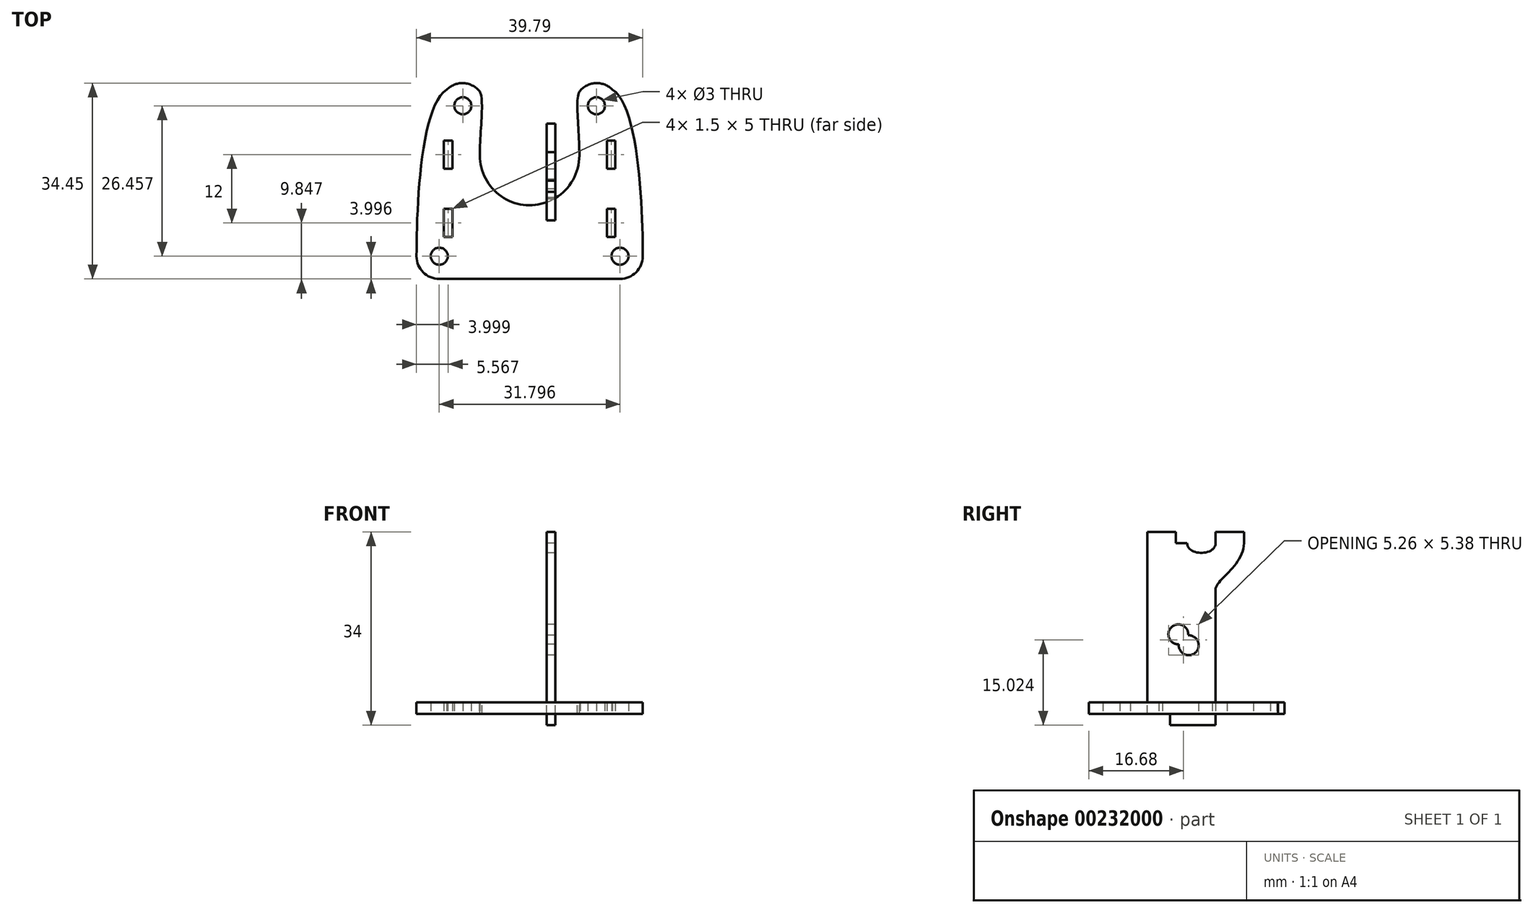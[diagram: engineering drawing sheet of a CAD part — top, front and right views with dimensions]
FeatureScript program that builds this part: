
annotation { "Feature Type Name" : "Feature", "Feature Type Description" : "" }
export const myFeature = defineFeature(function(context is Context, id is Id, definition is map)
    precondition{}
    {
        {
            var Q0;
            Q0=qCreatedBy(makeId("Right.planeOp"),FACE);
            var sketch = newSketch(context, id + "F0", { "sketchPlane" : qUnion([Q0])});
            skLineSegment(sketch, "E0", {"start": v(30.57, 0) * mm, "end": v(30.57, -2) * mm});
            skLineSegment(sketch, "E1", {"start": v(30.57, -2) * mm, "end": v(22.57, -2) * mm});
            skLineSegment(sketch, "E2", {"start": v(22.57, -2) * mm, "end": v(22.57, 0) * mm});
            skLineSegment(sketch, "E3", {"start": v(22.57, 0) * mm, "end": v(18.57, 0) * mm});
            skLineSegment(sketch, "E4", {"start": v(18.57, 30) * mm, "end": v(18.57, 0) * mm});
            skArc(sketch, "E5", {"start": v(24.11, 12.24) * mm, "mid": v(27.06, 10.8) * mm, "end": v(25.77, 13.81) * mm});
            skPoint(sketch, "E5.centerSnap0", {"position": v(18.57, 15) * mm});
            skPoint(sketch, "E5.centerSnap1", {"position": v(26.57, 32) * mm});
            skArc(sketch, "E6", {"start": v(25.77, 13.81) * mm, "mid": v(22.82, 15.25) * mm, "end": v(24.11, 12.24) * mm});
            skLineSegment(sketch, "E7", {"start": v(18.57, 30) * mm, "end": v(18.57, 32) * mm});
            skLineSegment(sketch, "E8", {"start": v(18.57, 32) * mm, "end": v(23.57, 32) * mm});
            skLineSegment(sketch, "E9", {"start": v(30.57, 21.84) * mm, "end": v(30.57, 0) * mm});
            skFitSpline(sketch, "E10", {"points": [v(30.57, 30) * mm, v(25.57, 30) * mm], "startDerivative": vector(0, -6.72) * mm, "endDerivative": vector(0, 6.72) * mm});
            skLineSegment(sketch, "E11", {"start": v(27.95, 30) * mm, "end": v(27.95, 28) * mm, "construction": true});
            skLineSegment(sketch, "E12", {"start": v(30.57, 27.76) * mm, "end": v(25.57, 27.76) * mm, "construction": true});
            skLineSegment(sketch, "E13", {"start": v(30.57, 30) * mm, "end": v(30.57, 32) * mm});
            skLineSegment(sketch, "E14", {"start": v(30.57, 32) * mm, "end": v(35.57, 32) * mm});
            skLineSegment(sketch, "E15", {"start": v(35.57, 32) * mm, "end": v(35.57, 30) * mm});
            skFitSpline(sketch, "E16", {"points": [v(35.57, 30) * mm, v(30.57, 21.84) * mm], "startDerivative": vector(0, -11.6) * mm, "endDerivative": vector(0, -5.4) * mm});
            skLineSegment(sketch, "E17", {"start": v(23.57, 32) * mm, "end": v(23.57, 30) * mm});
            skLineSegment(sketch, "E18", {"start": v(23.57, 30) * mm, "end": v(25.57, 30) * mm});
            skPoint(sketch, "E19", {"position": v(25.77, 13.81) * mm});
            skPoint(sketch, "E20", {"position": v(24.11, 12.24) * mm});
            skSolve(sketch);
        }
        {
            var Q0;
            Q0 = qSketchRegion(id + "F0", true);
            extrude(context, id + "F1", {"entities" : qUnion([Q0]), "depth" : 1.5 * mm});
        }
        {
            var Q0;
            Q0=qCreatedBy(makeId("Top.planeOp"),FACE);
            var sketch = newSketch(context, id + "F2", { "sketchPlane" : qUnion([Q0])});
            skPoint(sketch, "E21.middle", {"position": v(-3.02, -2.3) * mm});
            skLineSegment(sketch, "E22.bottom", {"start": v(22.68, 30.32) * mm, "end": v(-28.72, 30.32) * mm, "construction": true});
            skLineSegment(sketch, "E22.top", {"start": v(22.68, -34.92) * mm, "end": v(-28.72, -34.92) * mm, "construction": true});
            skLineSegment(sketch, "E22.left", {"start": v(22.68, 30.32) * mm, "end": v(22.68, -34.92) * mm, "construction": true});
            skLineSegment(sketch, "E22.right", {"start": v(-28.72, 30.32) * mm, "end": v(-28.72, -34.92) * mm, "construction": true});
            skLineSegment(sketch, "E23.bottom", {"start": v(-68.02, 80.2) * mm, "end": v(61.98, 80.2) * mm, "construction": true});
            skLineSegment(sketch, "E23.top", {"start": v(-68.02, -84.8) * mm, "end": v(61.98, -84.8) * mm, "construction": true});
            skLineSegment(sketch, "E23.left", {"start": v(-68.02, 80.2) * mm, "end": v(-68.02, -84.8) * mm, "construction": true});
            skLineSegment(sketch, "E23.right", {"start": v(61.98, 80.2) * mm, "end": v(61.98, -84.8) * mm, "construction": true});
            skCircle(sketch, "E24", {"center": v(61.98, 80.2) * mm, "radius": 4.5 * mm, "construction": true});
            skCircle(sketch, "E25", {"center": v(-68.02, 80.2) * mm, "radius": 4.5 * mm, "construction": true});
            skCircle(sketch, "E26", {"center": v(61.98, -84.8) * mm, "radius": 4.5 * mm, "construction": true});
            skCircle(sketch, "E27", {"center": v(-68.02, -84.8) * mm, "radius": 4.5 * mm, "construction": true});
            skCircle(sketch, "E28", {"center": v(61.98, 80.2) * mm, "radius": 8 * mm, "construction": true});
            skCircle(sketch, "E29", {"center": v(61.98, -84.8) * mm, "radius": 8 * mm, "construction": true});
            skCircle(sketch, "E30", {"center": v(-68.02, -84.8) * mm, "radius": 8 * mm, "construction": true});
            skCircle(sketch, "E31", {"center": v(-68.02, 80.2) * mm, "radius": 8 * mm, "construction": true});
            skCircle(sketch, "E32", {"center": v(61.98, 80.2) * mm, "radius": 9.5 * mm, "construction": true});
            skCircle(sketch, "E33", {"center": v(61.98, -84.8) * mm, "radius": 9.5 * mm, "construction": true});
            skCircle(sketch, "E34", {"center": v(-68.02, -84.8) * mm, "radius": 9.5 * mm, "construction": true});
            skCircle(sketch, "E35", {"center": v(-68.02, 80.2) * mm, "radius": 9.5 * mm, "construction": true});
            skCircle(sketch, "E36", {"center": v(61.98, 80.2) * mm, "radius": 14 * mm, "construction": true});
            skCircle(sketch, "E37", {"center": v(-68.02, 80.2) * mm, "radius": 14 * mm, "construction": true});
            skCircle(sketch, "E38", {"center": v(61.98, -84.8) * mm, "radius": 14 * mm, "construction": true});
            skCircle(sketch, "E39", {"center": v(-68.02, -84.8) * mm, "radius": 14 * mm, "construction": true});
            skCircle(sketch, "E40", {"center": v(61.98, 80.2) * mm, "radius": 63.5 * mm, "construction": true});
            skCircle(sketch, "E41", {"center": v(61.98, -84.8) * mm, "radius": 63.5 * mm, "construction": true});
            skCircle(sketch, "E42", {"center": v(-68.02, -84.8) * mm, "radius": 63.5 * mm, "construction": true});
            skCircle(sketch, "E43", {"center": v(-68.02, 80.2) * mm, "radius": 63.5 * mm, "construction": true});
            skLineSegment(sketch, "E44.bottom", {"start": v(-29.21, 23.9) * mm, "end": v(23.17, 23.9) * mm, "construction": true});
            skLineSegment(sketch, "E44.top", {"start": v(-29.21, -28.49) * mm, "end": v(23.17, -28.49) * mm, "construction": true});
            skLineSegment(sketch, "E44.left", {"start": v(-29.21, 23.9) * mm, "end": v(-29.21, -28.49) * mm, "construction": true});
            skLineSegment(sketch, "E44.right", {"start": v(23.17, 23.9) * mm, "end": v(23.17, -28.49) * mm, "construction": true});
            skCircle(sketch, "E45", {"center": v(22.68, 30.32) * mm, "radius": 1.5 * mm, "construction": true});
            skCircle(sketch, "E46", {"center": v(-28.72, 30.32) * mm, "radius": 1.5 * mm, "construction": true});
            skCircle(sketch, "E47", {"center": v(22.68, -34.92) * mm, "radius": 1.5 * mm, "construction": true});
            skCircle(sketch, "E48", {"center": v(-28.72, -34.92) * mm, "radius": 1.5 * mm, "construction": true});
            skLineSegment(sketch, "E49", {"start": v(-68.02, 80.2) * mm, "end": v(61.98, -84.8) * mm, "construction": true});
            skLineSegment(sketch, "E50", {"start": v(61.98, 80.2) * mm, "end": v(-68.02, -84.8) * mm, "construction": true});
            skLineSegment(sketch, "E51.bottom", {"start": v(-18.27, -7.32) * mm, "end": v(12.23, -7.32) * mm, "construction": true});
            skLineSegment(sketch, "E51.top", {"start": v(-18.27, -37.82) * mm, "end": v(12.23, -37.82) * mm, "construction": true});
            skLineSegment(sketch, "E51.left", {"start": v(-18.27, -7.32) * mm, "end": v(-18.27, -37.82) * mm, "construction": true});
            skLineSegment(sketch, "E51.right", {"start": v(12.23, -7.32) * mm, "end": v(12.23, -37.82) * mm, "construction": true});
            skPoint(sketch, "E51.middle", {"position": v(-3.02, -22.57) * mm});
            skLineSegment(sketch, "E52.bottom", {"start": v(-18.27, 29.18) * mm, "end": v(12.23, 29.18) * mm, "construction": true});
            skLineSegment(sketch, "E52.top", {"start": v(-18.27, -1.32) * mm, "end": v(12.23, -1.32) * mm, "construction": true});
            skLineSegment(sketch, "E52.left", {"start": v(-18.27, 29.18) * mm, "end": v(-18.27, -1.32) * mm, "construction": true});
            skLineSegment(sketch, "E52.right", {"start": v(12.23, 29.18) * mm, "end": v(12.23, -1.32) * mm, "construction": true});
            skPoint(sketch, "E52.middle", {"position": v(-3.02, 13.93) * mm});
            skLineSegment(sketch, "E53", {"start": v(-3.02, -1.32) * mm, "end": v(-3.02, -7.32) * mm, "construction": true});
            skLineSegment(sketch, "E54", {"start": v(-3.02, 38.71) * mm, "end": v(-14.77, 38.71) * mm, "construction": true});
            skLineSegment(sketch, "E55", {"start": v(-3.02, 38.71) * mm, "end": v(8.73, 38.71) * mm, "construction": true});
            skLineSegment(sketch, "E56", {"start": v(-28.72, 30.32) * mm, "end": v(-23.23, 34.65) * mm, "construction": true});
            skLineSegment(sketch, "E57", {"start": v(-28.72, 30.32) * mm, "end": v(-34.22, 25.99) * mm, "construction": true});
            skLineSegment(sketch, "E58", {"start": v(-28.72, 30.32) * mm, "end": v(-33.06, 35.82) * mm, "construction": true});
            skLineSegment(sketch, "E59", {"start": v(22.68, 30.32) * mm, "end": v(27.01, 35.82) * mm, "construction": true});
            skLineSegment(sketch, "E60", {"start": v(22.68, 30.32) * mm, "end": v(17.18, 34.65) * mm, "construction": true});
            skLineSegment(sketch, "E61", {"start": v(22.68, 30.32) * mm, "end": v(28.18, 25.99) * mm, "construction": true});
            skLineSegment(sketch, "E62", {"start": v(22.68, -34.92) * mm, "end": v(27.01, -40.42) * mm, "construction": true});
            skLineSegment(sketch, "E63", {"start": v(22.68, -34.92) * mm, "end": v(17.18, -39.25) * mm, "construction": true});
            skLineSegment(sketch, "E64", {"start": v(22.68, -34.92) * mm, "end": v(28.18, -30.59) * mm, "construction": true});
            skLineSegment(sketch, "E65", {"start": v(-28.72, -34.92) * mm, "end": v(-33.06, -40.42) * mm, "construction": true});
            skLineSegment(sketch, "E66", {"start": v(-28.72, -34.92) * mm, "end": v(-23.23, -39.25) * mm, "construction": true});
            skLineSegment(sketch, "E67", {"start": v(-28.72, -34.92) * mm, "end": v(-34.22, -30.59) * mm, "construction": true});
            skFitSpline(sketch, "E68", {"points": [v(-23.23, 34.65) * mm, v(-33.06, 35.82) * mm, v(-34.22, 25.99) * mm], "startDerivative": vector(-20.3, 7.46) * mm, "endDerivative": vector(0.93, -21.61) * mm});
            skFitSpline(sketch, "E69", {"points": [v(17.18, 34.65) * mm, v(27.01, 35.82) * mm, v(28.18, 25.99) * mm], "startDerivative": vector(20.3, 7.46) * mm, "endDerivative": vector(-0.93, -21.61) * mm});
            skFitSpline(sketch, "E70", {"points": [v(28.18, -30.59) * mm, v(27.01, -40.42) * mm, v(17.18, -39.25) * mm], "startDerivative": vector(0.93, -21.61) * mm, "endDerivative": vector(-20.3, 7.46) * mm});
            skFitSpline(sketch, "E71", {"points": [v(-23.23, -39.25) * mm, v(-33.06, -40.42) * mm, v(-34.22, -30.59) * mm], "startDerivative": vector(-20.3, -7.46) * mm, "endDerivative": vector(0.93, 21.61) * mm});
            skLineSegment(sketch, "E72", {"start": v(-14.77, 38.71) * mm, "end": v(-18.77, 38.71) * mm, "construction": true});
            skLineSegment(sketch, "E73", {"start": v(8.73, 38.71) * mm, "end": v(12.73, 38.71) * mm, "construction": true});
            skCircle(sketch, "E74", {"center": v(-14.77, 38.71) * mm, "radius": 1.5 * mm});
            skCircle(sketch, "E75", {"center": v(8.73, 38.71) * mm, "radius": 1.5 * mm});
            skLineSegment(sketch, "E76", {"start": v(-3.02, 38.71) * mm, "end": v(-3.02, 42.71) * mm, "construction": true});
            skLineSegment(sketch, "E77", {"start": v(-18.77, 38.71) * mm, "end": v(-18.77, 38.71) * mm});
            skLineSegment(sketch, "E78", {"start": v(-14.77, 42.71) * mm, "end": v(-3.02, 42.71) * mm});
            skLineSegment(sketch, "E79", {"start": v(-3.02, 42.71) * mm, "end": v(8.73, 42.71) * mm});
            skLineSegment(sketch, "E80", {"start": v(12.73, 38.71) * mm, "end": v(12.73, 38.71) * mm});
            skPoint(sketch, "E81.visualSharp", {"position": v(-18.77, 42.71) * mm});
            skArc(sketch, "E81.filletArc", {"start": v(-14.77, 42.71) * mm, "mid": v(-17.6, 41.54) * mm, "end": v(-18.77, 38.71) * mm});
            skPoint(sketch, "E82.visualSharp", {"position": v(12.73, 42.71) * mm});
            skArc(sketch, "E82.filletArc", {"start": v(12.73, 38.71) * mm, "mid": v(11.56, 41.54) * mm, "end": v(8.73, 42.71) * mm});
            skLineSegment(sketch, "E83", {"start": v(-23.23, 34.65) * mm, "end": v(-21.36, 34.08) * mm});
            skLineSegment(sketch, "E84", {"start": v(-18.77, 36) * mm, "end": v(-18.77, 38.71) * mm});
            skPoint(sketch, "E85.visualSharp", {"position": v(-18.77, 33.29) * mm});
            skArc(sketch, "E85.filletArc", {"start": v(-21.36, 34.08) * mm, "mid": v(-19.58, 34.38) * mm, "end": v(-18.77, 36) * mm});
            skLineSegment(sketch, "E86", {"start": v(-18.77, 33.29) * mm, "end": v(-3.02, 33.29) * mm, "construction": true});
            skLineSegment(sketch, "E87", {"start": v(-3.02, 33.29) * mm, "end": v(12.73, 33.29) * mm, "construction": true});
            skLineSegment(sketch, "E88", {"start": v(17.18, 34.65) * mm, "end": v(15.31, 34.08) * mm});
            skLineSegment(sketch, "E89", {"start": v(12.73, 38.71) * mm, "end": v(12.73, 36) * mm});
            skPoint(sketch, "E90.visualSharp", {"position": v(12.73, 33.29) * mm});
            skArc(sketch, "E90.filletArc", {"start": v(12.73, 36) * mm, "mid": v(13.54, 34.38) * mm, "end": v(15.31, 34.08) * mm});
            skCircle(sketch, "E91", {"center": v(-18.27, -37.82) * mm, "radius": 1.5 * mm});
            skCircle(sketch, "E92", {"center": v(12.23, -37.82) * mm, "radius": 1.5 * mm});
            skLineSegment(sketch, "E93", {"start": v(-3.02, -37.82) * mm, "end": v(-3.02, -41.82) * mm, "construction": true});
            skLineSegment(sketch, "E94", {"start": v(-18.27, -37.82) * mm, "end": v(-22.27, -37.82) * mm, "construction": true});
            skLineSegment(sketch, "E95", {"start": v(12.23, -37.82) * mm, "end": v(16.23, -37.82) * mm, "construction": true});
            skLineSegment(sketch, "E96", {"start": v(-22.27, -40.76) * mm, "end": v(-3.02, -40.76) * mm, "construction": true});
            skLineSegment(sketch, "E97", {"start": v(-3.02, -40.76) * mm, "end": v(16.23, -40.76) * mm, "construction": true});
            skPoint(sketch, "E98.visualSharp", {"position": v(-22.27, -40.76) * mm});
            skPoint(sketch, "E99.visualSharp", {"position": v(16.23, -40.76) * mm});
            skCircle(sketch, "E100", {"center": v(-12.82, -47.2) * mm, "radius": 1.5 * mm});
            skCircle(sketch, "E101", {"center": v(6.78, -47.2) * mm, "radius": 1.5 * mm});
            skLineSegment(sketch, "E102", {"start": v(-12.82, -47.2) * mm, "end": v(-3.02, -47.2) * mm, "construction": true});
            skLineSegment(sketch, "E103", {"start": v(-3.02, -47.2) * mm, "end": v(6.78, -47.2) * mm, "construction": true});
            skFitSpline(sketch, "E104", {"points": [v(-34.22, 25.99) * mm, v(-28.72, -2.3) * mm, v(-34.22, -30.59) * mm], "startDerivative": vector(16.96, -67.18) * mm, "endDerivative": vector(-16.96, -67.18) * mm});
            skFitSpline(sketch, "E105", {"points": [v(28.18, 25.99) * mm, v(22.68, -2.3) * mm, v(28.18, -30.59) * mm], "startDerivative": vector(-16.96, -67.18) * mm, "endDerivative": vector(16.96, -67.18) * mm});
            skLineSegment(sketch, "E106", {"start": v(-3.02, -47.2) * mm, "end": v(-3.02, -53.2) * mm, "construction": true});
            skLineSegment(sketch, "E107", {"start": v(-12.82, -47.2) * mm, "end": v(-16.82, -47.2) * mm, "construction": true});
            skLineSegment(sketch, "E108", {"start": v(-12.82, -47.2) * mm, "end": v(-12.82, -51.2) * mm, "construction": true});
            skLineSegment(sketch, "E109", {"start": v(6.78, -47.2) * mm, "end": v(10.78, -47.2) * mm, "construction": true});
            skLineSegment(sketch, "E110", {"start": v(6.78, -47.2) * mm, "end": v(6.78, -51.2) * mm, "construction": true});
            skCircle(sketch, "E111", {"center": v(-28.72, 30.32) * mm, "radius": 1.5 * mm});
            skCircle(sketch, "E112", {"center": v(22.68, 30.32) * mm, "radius": 1.5 * mm});
            skCircle(sketch, "E113", {"center": v(-28.72, -34.92) * mm, "radius": 1.5 * mm});
            skCircle(sketch, "E114", {"center": v(22.68, -34.92) * mm, "radius": 1.5 * mm});
            skLineSegment(sketch, "E115", {"start": v(-3.02, 30.32) * mm, "end": v(-3.02, 38.71) * mm, "construction": true});
            skLineSegment(sketch, "E116", {"start": v(114.53, -26.93) * mm, "end": v(114.53, 7.03) * mm, "construction": true});
            skLineSegment(sketch, "E117", {"start": v(-22.07, -38.82) * mm, "end": v(-3.02, -38.82) * mm, "construction": true});
            skLineSegment(sketch, "E118", {"start": v(-3.02, -38.82) * mm, "end": v(16.02, -38.82) * mm, "construction": true});
            skFitSpline(sketch, "E119", {"points": [v(-22.27, -40.76) * mm, v(-16.82, -47.2) * mm, v(-12.82, -51.2) * mm, v(-3.02, -53.2) * mm], "startDerivative": vector(17.01, -18.5) * mm, "endDerivative": vector(29.8, -3.11) * mm});
            skFitSpline(sketch, "E120", {"points": [v(16.23, -40.76) * mm, v(10.78, -47.2) * mm, v(6.78, -51.2) * mm, v(-3.02, -53.2) * mm], "startDerivative": vector(-17.98, -19.6) * mm, "endDerivative": vector(-29.8, -3.11) * mm});
            skLineSegment(sketch, "E121", {"start": v(115.56, 8.03) * mm, "end": v(168.77, 6.38) * mm, "construction": true});
            skPoint(sketch, "E122.visualSharp", {"position": v(114.53, 8.07) * mm});
            skArc(sketch, "E122.filletArc", {"start": v(115.56, 8.03) * mm, "mid": v(114.83, 7.75) * mm, "end": v(114.53, 7.03) * mm, "construction": true});
            skPoint(sketch, "E123.visualSharp", {"position": v(16.02, -38.82) * mm});
            skPoint(sketch, "E124.visualSharp", {"position": v(-22.07, -38.82) * mm});
            skLineSegment(sketch, "E125.bottom", {"start": v(-16.8, 15.2) * mm, "end": v(10.76, 15.2) * mm, "construction": true});
            skLineSegment(sketch, "E125.top", {"start": v(-16.8, -19.8) * mm, "end": v(10.76, -19.8) * mm, "construction": true});
            skLineSegment(sketch, "E125.left", {"start": v(-16.8, 15.2) * mm, "end": v(-16.8, -19.8) * mm, "construction": true});
            skLineSegment(sketch, "E125.right", {"start": v(10.76, 15.2) * mm, "end": v(10.76, -19.8) * mm, "construction": true});
            skCircle(sketch, "E126", {"center": v(-18.27, -7.32) * mm, "radius": 1.5 * mm});
            skCircle(sketch, "E127", {"center": v(12.23, -7.32) * mm, "radius": 1.5 * mm});
            skCircle(sketch, "E128", {"center": v(12.23, -1.32) * mm, "radius": 1.5 * mm});
            skCircle(sketch, "E129", {"center": v(-18.27, -1.32) * mm, "radius": 1.5 * mm});
            skCircle(sketch, "E130", {"center": v(-18.27, 29.18) * mm, "radius": 1.5 * mm});
            skCircle(sketch, "E131", {"center": v(12.23, 29.18) * mm, "radius": 1.5 * mm});
            skFitSpline(sketch, "E132", {"points": [v(-23.23, -39.25) * mm, v(-22.27, -40.76) * mm], "startDerivative": vector(0.95, -1.5) * mm, "endDerivative": vector(0.95, -1.5) * mm});
            skFitSpline(sketch, "E133", {"points": [v(17.18, -39.25) * mm, v(16.23, -40.76) * mm], "startDerivative": vector(-0.95, -1.5) * mm, "endDerivative": vector(-0.95, -1.5) * mm});
            skLineSegment(sketch, "E134", {"start": v(-3.02, 10.77) * mm, "end": v(-21.23, 10.77) * mm, "construction": true});
            skLineSegment(sketch, "E135", {"start": v(-3.02, 10.77) * mm, "end": v(15.18, 10.77) * mm, "construction": true});
            skLineSegment(sketch, "E136", {"start": v(-3.02, -2.3) * mm, "end": v(-3.02, 11.97) * mm, "construction": true});
            skLineSegment(sketch, "E137", {"start": v(-3.02, -2.3) * mm, "end": v(10.3, -2.3) * mm, "construction": true});
            skLineSegment(sketch, "E138.bottom", {"start": v(-18.92, 12.26) * mm, "end": v(12.87, 12.26) * mm, "construction": true});
            skLineSegment(sketch, "E138.top", {"start": v(-18.92, -16.85) * mm, "end": v(12.87, -16.85) * mm, "construction": true});
            skLineSegment(sketch, "E138.left", {"start": v(-18.92, 12.26) * mm, "end": v(-18.92, -16.85) * mm, "construction": true});
            skLineSegment(sketch, "E138.right", {"start": v(12.87, 12.26) * mm, "end": v(12.87, -16.85) * mm, "construction": true});
            skCircle(sketch, "E139", {"center": v(12.87, 12.26) * mm, "radius": 1.5 * mm});
            skCircle(sketch, "E140", {"center": v(12.87, -16.85) * mm, "radius": 1.5 * mm});
            skCircle(sketch, "E141", {"center": v(-18.92, -16.85) * mm, "radius": 1.5 * mm});
            skCircle(sketch, "E142", {"center": v(-18.92, 12.26) * mm, "radius": 1.5 * mm});
            skLineSegment(sketch, "E143", {"start": v(-3.02, 23.62) * mm, "end": v(11.3, 23.62) * mm, "construction": true});
            skLineSegment(sketch, "E144", {"start": v(-3.02, 23.62) * mm, "end": v(-17.35, 23.62) * mm, "construction": true});
            skLineSegment(sketch, "E145.bottom", {"start": v(-18.1, 27.62) * mm, "end": v(-16.6, 27.62) * mm});
            skLineSegment(sketch, "E145.top", {"start": v(-18.1, 19.62) * mm, "end": v(-16.6, 19.62) * mm});
            skLineSegment(sketch, "E145.left", {"start": v(-18.1, 27.62) * mm, "end": v(-18.1, 19.62) * mm});
            skLineSegment(sketch, "E145.right", {"start": v(-16.6, 27.62) * mm, "end": v(-16.6, 19.62) * mm});
            skPoint(sketch, "E145.middle", {"position": v(-17.35, 23.62) * mm});
            skLineSegment(sketch, "E146.bottom", {"start": v(12.06, 27.62) * mm, "end": v(10.56, 27.62) * mm});
            skLineSegment(sketch, "E146.top", {"start": v(12.06, 19.62) * mm, "end": v(10.56, 19.62) * mm});
            skLineSegment(sketch, "E146.left", {"start": v(12.06, 27.62) * mm, "end": v(12.06, 19.62) * mm});
            skLineSegment(sketch, "E146.right", {"start": v(10.56, 27.62) * mm, "end": v(10.56, 19.62) * mm});
            skPoint(sketch, "E146.middle", {"position": v(11.3, 23.62) * mm});
            skSolve(sketch);
        }
        {
            var Q0;
            Q0=qCreatedBy(makeId("Top.planeOp"),FACE);
            var sketch = newSketch(context, id + "F3", { "sketchPlane" : qUnion([Q0])});
            skCircle(sketch, "E147", {"center": v(-18.92, 12.26) * mm, "radius": 4 * mm, "construction": true});
            skCircle(sketch, "E148", {"center": v(12.87, 12.26) * mm, "radius": 4 * mm, "construction": true});
            skCircle(sketch, "E149", {"center": v(-14.77, 38.71) * mm, "radius": 4 * mm, "construction": true});
            skCircle(sketch, "E150", {"center": v(8.73, 38.71) * mm, "radius": 4 * mm, "construction": true});
            skLineSegment(sketch, "E151", {"start": v(-3.02, 38.71) * mm, "end": v(-18.77, 38.71) * mm, "construction": true});
            skLineSegment(sketch, "E152", {"start": v(-3.02, 38.71) * mm, "end": v(12.73, 38.71) * mm, "construction": true});
            skLineSegment(sketch, "E153", {"start": v(-18.92, 12.26) * mm, "end": v(-22.92, 12.26) * mm, "construction": true});
            skLineSegment(sketch, "E154", {"start": v(12.87, 12.26) * mm, "end": v(16.87, 12.26) * mm, "construction": true});
            skLineSegment(sketch, "E155", {"start": v(-18.92, 12.26) * mm, "end": v(-18.92, 8.26) * mm, "construction": true});
            skLineSegment(sketch, "E156", {"start": v(12.87, 12.26) * mm, "end": v(12.87, 8.26) * mm, "construction": true});
            skFitSpline(sketch, "E157", {"points": [v(-18.92, 8.26) * mm, v(12.87, 8.26) * mm], "startDerivative": vector(31.8, 0) * mm, "endDerivative": vector(31.8, 0) * mm});
            skArc(sketch, "E158", {"start": v(-22.92, 12.26) * mm, "mid": v(-21.75, 9.43) * mm, "end": v(-18.92, 8.26) * mm});
            skArc(sketch, "E159", {"start": v(12.87, 8.26) * mm, "mid": v(15.7, 9.43) * mm, "end": v(16.87, 12.26) * mm});
            skLineSegment(sketch, "E160", {"start": v(-14.77, 38.71) * mm, "end": v(-14.77, 42.71) * mm, "construction": true});
            skLineSegment(sketch, "E161", {"start": v(8.73, 38.71) * mm, "end": v(8.73, 42.71) * mm, "construction": true});
            skLineSegment(sketch, "E162", {"start": v(-3.02, 41.37) * mm, "end": v(-11.92, 41.37) * mm, "construction": true});
            skLineSegment(sketch, "E163", {"start": v(-3.02, 41.37) * mm, "end": v(5.88, 41.37) * mm, "construction": true});
            skCircle(sketch, "E164", {"center": v(-3.02, 29.97) * mm, "radius": 8.75 * mm, "construction": true});
            skLineSegment(sketch, "E165", {"start": v(-3.02, 29.97) * mm, "end": v(-11.77, 29.97) * mm, "construction": true});
            skLineSegment(sketch, "E166", {"start": v(-3.02, 29.97) * mm, "end": v(5.73, 29.97) * mm, "construction": true});
            skArc(sketch, "E167", {"start": v(-11.77, 29.97) * mm, "mid": v(-3.02, 21.22) * mm, "end": v(5.73, 29.97) * mm});
            skArc(sketch, "E168", {"start": v(-11.92, 41.37) * mm, "mid": v(-13.21, 42.33) * mm, "end": v(-14.77, 42.71) * mm});
            skArc(sketch, "E169", {"start": v(8.73, 42.71) * mm, "mid": v(7.16, 42.33) * mm, "end": v(5.88, 41.37) * mm});
            skFitSpline(sketch, "E170", {"points": [v(-11.92, 41.37) * mm, v(-11.77, 29.97) * mm], "startDerivative": vector(3.21, -3.13) * mm, "endDerivative": vector(0.15, -12.72) * mm});
            skFitSpline(sketch, "E171", {"points": [v(5.73, 29.97) * mm, v(5.88, 41.37) * mm], "startDerivative": vector(0.15, 12.72) * mm, "endDerivative": vector(3.21, 3.13) * mm});
            skLineSegment(sketch, "E172", {"start": v(-10.85, 40.33) * mm, "end": v(-3.02, 40.33) * mm, "construction": true});
            skLineSegment(sketch, "E173", {"start": v(-3.02, 40.33) * mm, "end": v(4.8, 40.33) * mm, "construction": true});
            skCircle(sketch, "E174", {"center": v(-14.77, 38.71) * mm, "radius": 1.5 * mm});
            skCircle(sketch, "E175", {"center": v(8.73, 38.71) * mm, "radius": 1.5 * mm});
            skCircle(sketch, "E176", {"center": v(12.87, 12.26) * mm, "radius": 1.5 * mm});
            skCircle(sketch, "E177", {"center": v(-18.92, 12.26) * mm, "radius": 1.5 * mm});
            skLineSegment(sketch, "E178", {"start": v(-41.24, 35.23) * mm, "end": v(-41.24, 5.23) * mm, "construction": true});
            skLineSegment(sketch, "E179", {"start": v(-3.02, 30.1) * mm, "end": v(-17.35, 30.1) * mm, "construction": true});
            skLineSegment(sketch, "E180.bottom", {"start": v(-18.1, 32.6) * mm, "end": v(-16.6, 32.6) * mm});
            skLineSegment(sketch, "E180.top", {"start": v(-18.1, 27.6) * mm, "end": v(-16.6, 27.6) * mm});
            skLineSegment(sketch, "E180.left", {"start": v(-18.1, 32.6) * mm, "end": v(-18.1, 27.6) * mm});
            skLineSegment(sketch, "E180.right", {"start": v(-16.6, 32.6) * mm, "end": v(-16.6, 27.6) * mm});
            skPoint(sketch, "E180.middle", {"position": v(-17.35, 30.1) * mm});
            skLineSegment(sketch, "E181", {"start": v(-3.02, 30.1) * mm, "end": v(11.3, 30.1) * mm, "construction": true});
            skLineSegment(sketch, "E182.bottom", {"start": v(12.06, 32.6) * mm, "end": v(10.56, 32.6) * mm});
            skLineSegment(sketch, "E182.top", {"start": v(12.06, 27.6) * mm, "end": v(10.56, 27.6) * mm});
            skLineSegment(sketch, "E182.left", {"start": v(12.06, 32.6) * mm, "end": v(12.06, 27.6) * mm});
            skLineSegment(sketch, "E182.right", {"start": v(10.56, 32.6) * mm, "end": v(10.56, 27.6) * mm});
            skPoint(sketch, "E182.middle", {"position": v(11.3, 30.1) * mm});
            skLineSegment(sketch, "E183", {"start": v(-16.6, 27.6) * mm, "end": v(-16.6, 20.6) * mm, "construction": true});
            skLineSegment(sketch, "E184.bottom", {"start": v(-16.6, 20.6) * mm, "end": v(-18.1, 20.6) * mm});
            skLineSegment(sketch, "E184.top", {"start": v(-16.6, 15.6) * mm, "end": v(-18.1, 15.6) * mm});
            skLineSegment(sketch, "E184.left", {"start": v(-16.6, 20.6) * mm, "end": v(-16.6, 15.6) * mm});
            skLineSegment(sketch, "E184.right", {"start": v(-18.1, 20.6) * mm, "end": v(-18.1, 15.6) * mm});
            skLineSegment(sketch, "E185", {"start": v(10.56, 27.6) * mm, "end": v(10.56, 20.6) * mm, "construction": true});
            skLineSegment(sketch, "E186.bottom", {"start": v(10.56, 20.6) * mm, "end": v(12.06, 20.6) * mm});
            skLineSegment(sketch, "E186.top", {"start": v(10.56, 15.6) * mm, "end": v(12.06, 15.6) * mm});
            skLineSegment(sketch, "E186.left", {"start": v(10.56, 20.6) * mm, "end": v(10.56, 15.6) * mm});
            skLineSegment(sketch, "E186.right", {"start": v(12.06, 20.6) * mm, "end": v(12.06, 15.6) * mm});
            skLineSegment(sketch, "E187", {"start": v(-14.77, 38.71) * mm, "end": v(-18.16, 42.1) * mm, "construction": true});
            skLineSegment(sketch, "E188", {"start": v(8.73, 38.71) * mm, "end": v(12.56, 42.54) * mm, "construction": true});
            skArc(sketch, "E189", {"start": v(11.56, 41.54) * mm, "mid": v(10.26, 42.4) * mm, "end": v(8.73, 42.71) * mm});
            skArc(sketch, "E190", {"start": v(-14.77, 42.71) * mm, "mid": v(-16.3, 42.4) * mm, "end": v(-17.6, 41.54) * mm});
            skFitSpline(sketch, "E191", {"points": [v(-22.92, 12.26) * mm, v(-17.6, 41.54) * mm], "startDerivative": vector(0, 25.05) * mm, "endDerivative": vector(14.01, 8.49) * mm});
            skFitSpline(sketch, "E192", {"points": [v(16.87, 12.26) * mm, v(11.56, 41.54) * mm], "startDerivative": vector(0, 25.05) * mm, "endDerivative": vector(-14.01, 8.49) * mm});
            skLineSegment(sketch, "E193", {"start": v(-18.77, 38.71) * mm, "end": v(-22.27, 38.71) * mm, "construction": true});
            skLineSegment(sketch, "E194", {"start": v(12.73, 38.71) * mm, "end": v(16.23, 38.71) * mm, "construction": true});
            skSolve(sketch);
        }
        {
            var Q0;
            Q0 = qSketchRegion(id + "F3", true);
            extrude(context, id + "F4", {"entities" : qUnion([Q0]), "depth" : 2 * mm});
        }
    });
